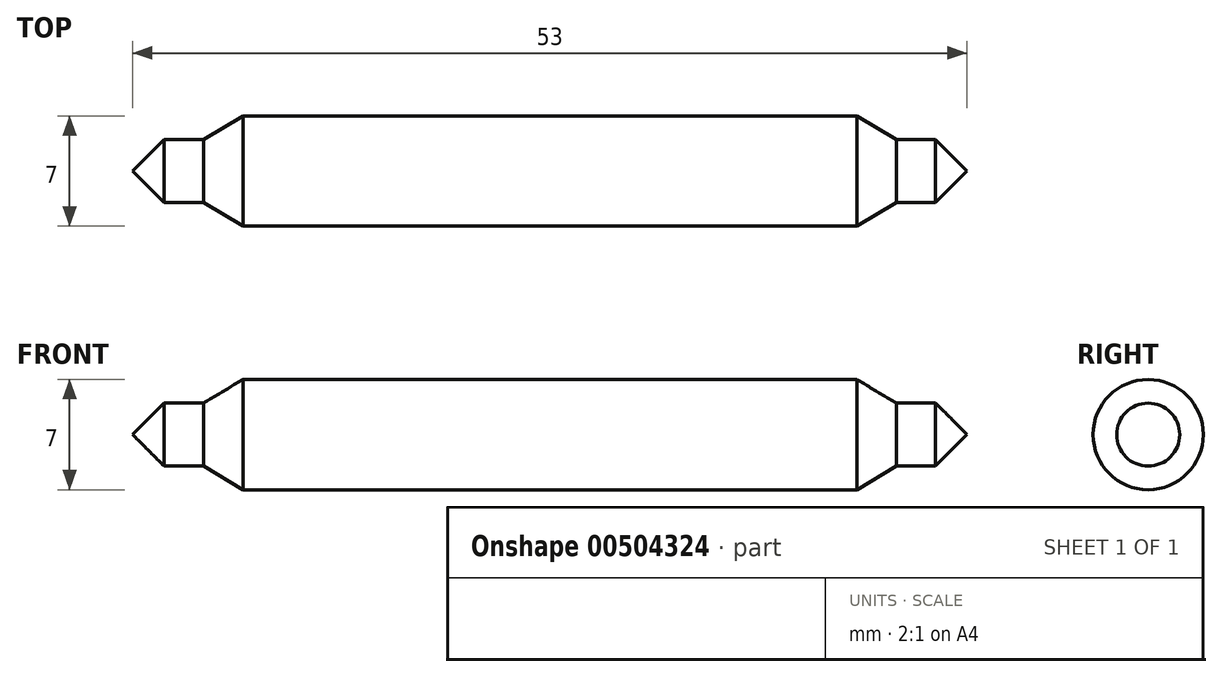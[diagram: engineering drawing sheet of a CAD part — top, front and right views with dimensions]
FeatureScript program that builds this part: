
annotation { "Feature Type Name" : "Feature", "Feature Type Description" : "" }
export const myFeature = defineFeature(function(context is Context, id is Id, definition is map)
    precondition{}
    {
        {
            var Q0;
            Q0=qCreatedBy(makeId("Front.planeOp"),FACE);
            var sketch = newSketch(context, id + "F0", { "sketchPlane" : qUnion([Q0])});
            skLineSegment(sketch, "E0.bottom", {"start": v(19.5, 3.5) * mm, "end": v(-19.5, 3.5) * mm});
            skLineSegment(sketch, "E0.top", {"start": v(19.5, -3.5) * mm, "end": v(-19.5, -3.5) * mm});
            skLineSegment(sketch, "E0.left", {"start": v(19.5, 3.5) * mm, "end": v(19.5, -3.5) * mm});
            skLineSegment(sketch, "E0.right", {"start": v(-19.5, 3.5) * mm, "end": v(-19.5, -3.5) * mm});
            skPoint(sketch, "E0.middle", {"position": v(0, 0) * mm});
            skLineSegment(sketch, "E1", {"start": v(-37.56, 0) * mm, "end": v(31.76, 0) * mm, "construction": true});
            skLineSegment(sketch, "E2.bottom", {"start": v(24.5, 2) * mm, "end": v(-24.5, 2) * mm});
            skLineSegment(sketch, "E2.top", {"start": v(24.5, -2) * mm, "end": v(-24.5, -2) * mm});
            skLineSegment(sketch, "E2.left", {"start": v(24.5, 2) * mm, "end": v(24.5, -2) * mm});
            skLineSegment(sketch, "E2.right", {"start": v(-24.5, 2) * mm, "end": v(-24.5, -2) * mm});
            skLineSegment(sketch, "E3", {"start": v(-24.5, 2) * mm, "end": v(-26.5, 0) * mm});
            skLineSegment(sketch, "E4", {"start": v(-26.5, 0) * mm, "end": v(26.5, 0) * mm});
            skLineSegment(sketch, "E5", {"start": v(26.5, 0) * mm, "end": v(24.5, 2) * mm});
            skLineSegment(sketch, "E6", {"start": v(22, 2) * mm, "end": v(19.5, 3.5) * mm});
            skLineSegment(sketch, "E7", {"start": v(-22, 2) * mm, "end": v(-19.5, 3.5) * mm});
            skSolve(sketch);
        }
        {
            var Q0;
            {var subQ0=sQuery(id+"F0.wireOp",EDGE,"E3");Q0=makeQuery(id+"F0.imprint","IMPRINT",FACE,{"disambiguationData":[TD([[makeQuery(id+"F0.imprint","IMPRINT",EDGE,{"derivedFrom":subQ0}),1.0]])]});}
            var Q1;
            {var subQ1=sQuery(id+"F0.wireOp",EDGE,"E2.bottom");var subQ6=sQuery(id+"F0.wireOp",EDGE,"E0.right");var subQ7=makeQuery(id+"F0.imprint","INTERSECT",VERTEX,{"derivedFrom":[subQ6,subQ1]});Q1=makeQuery(id+"F0.imprint","IMPRINT",FACE,{"disambiguationData":[TD([[makeQuery(id+"F0.imprint","IMPRINT",EDGE,{"disambiguationData":[TD([[subQ7,-1.0]])],"derivedFrom":subQ6}),-1.0]])]});}
            var Q2;
            {var subQ0=sQuery(id+"F0.wireOp",EDGE,"E7");Q2=makeQuery(id+"F0.imprint","IMPRINT",FACE,{"disambiguationData":[TD([[makeQuery(id+"F0.imprint","IMPRINT",EDGE,{"derivedFrom":subQ0}),-1.0]])]});}
            var Q3;
            {var subQ0=sQuery(id+"F0.wireOp",EDGE,"E0.bottom");Q3=makeQuery(id+"F0.imprint","IMPRINT",FACE,{"disambiguationData":[TD([[makeQuery(id+"F0.imprint","IMPRINT",EDGE,{"derivedFrom":subQ0}),1.0]])]});}
            var Q4;
            {var subQ0=sQuery(id+"F0.wireOp",EDGE,"E2.bottom");var subQ1=sQuery(id+"F0.wireOp",EDGE,"E0.left");var subQ2=makeQuery(id+"F0.imprint","INTERSECT",VERTEX,{"derivedFrom":[subQ1,subQ0]});Q4=makeQuery(id+"F0.imprint","IMPRINT",FACE,{"disambiguationData":[TD([[makeQuery(id+"F0.imprint","IMPRINT",EDGE,{"disambiguationData":[TD([[subQ2,-1.0]])],"derivedFrom":subQ1}),-1.0]])]});}
            var Q5;
            {var subQ0=sQuery(id+"F0.wireOp",EDGE,"E2.bottom");var subQ2=sQuery(id+"F0.wireOp",EDGE,"E0.left");var subQ3=makeQuery(id+"F0.imprint","INTERSECT",VERTEX,{"derivedFrom":[subQ2,subQ0]});Q5=makeQuery(id+"F0.imprint","IMPRINT",FACE,{"disambiguationData":[TD([[makeQuery(id+"F0.imprint","IMPRINT",EDGE,{"disambiguationData":[TD([[subQ3,-1.0]])],"derivedFrom":subQ2}),1.0]])]});}
            var Q6;
            {var subQ0=sQuery(id+"F0.wireOp",EDGE,"E6");Q6=makeQuery(id+"F0.imprint","IMPRINT",FACE,{"disambiguationData":[TD([[makeQuery(id+"F0.imprint","IMPRINT",EDGE,{"derivedFrom":subQ0}),1.0]])]});}
            var Q7;
            {var subQ0=sQuery(id+"F0.wireOp",EDGE,"E5");Q7=makeQuery(id+"F0.imprint","IMPRINT",FACE,{"disambiguationData":[TD([[makeQuery(id+"F0.imprint","IMPRINT",EDGE,{"derivedFrom":subQ0}),1.0]])]});}
            var Q8;
            Q8=sQuery(id+"F0.wireOp",EDGE,"E1");
            revolve(context, id + "F1", {"entities" : qUnion([Q0, Q1, Q2, Q3, Q4, Q5, Q6, Q7]), "axis" : qUnion([Q8]), "revolveType" : RevolveType.FULL});
        }
    });
